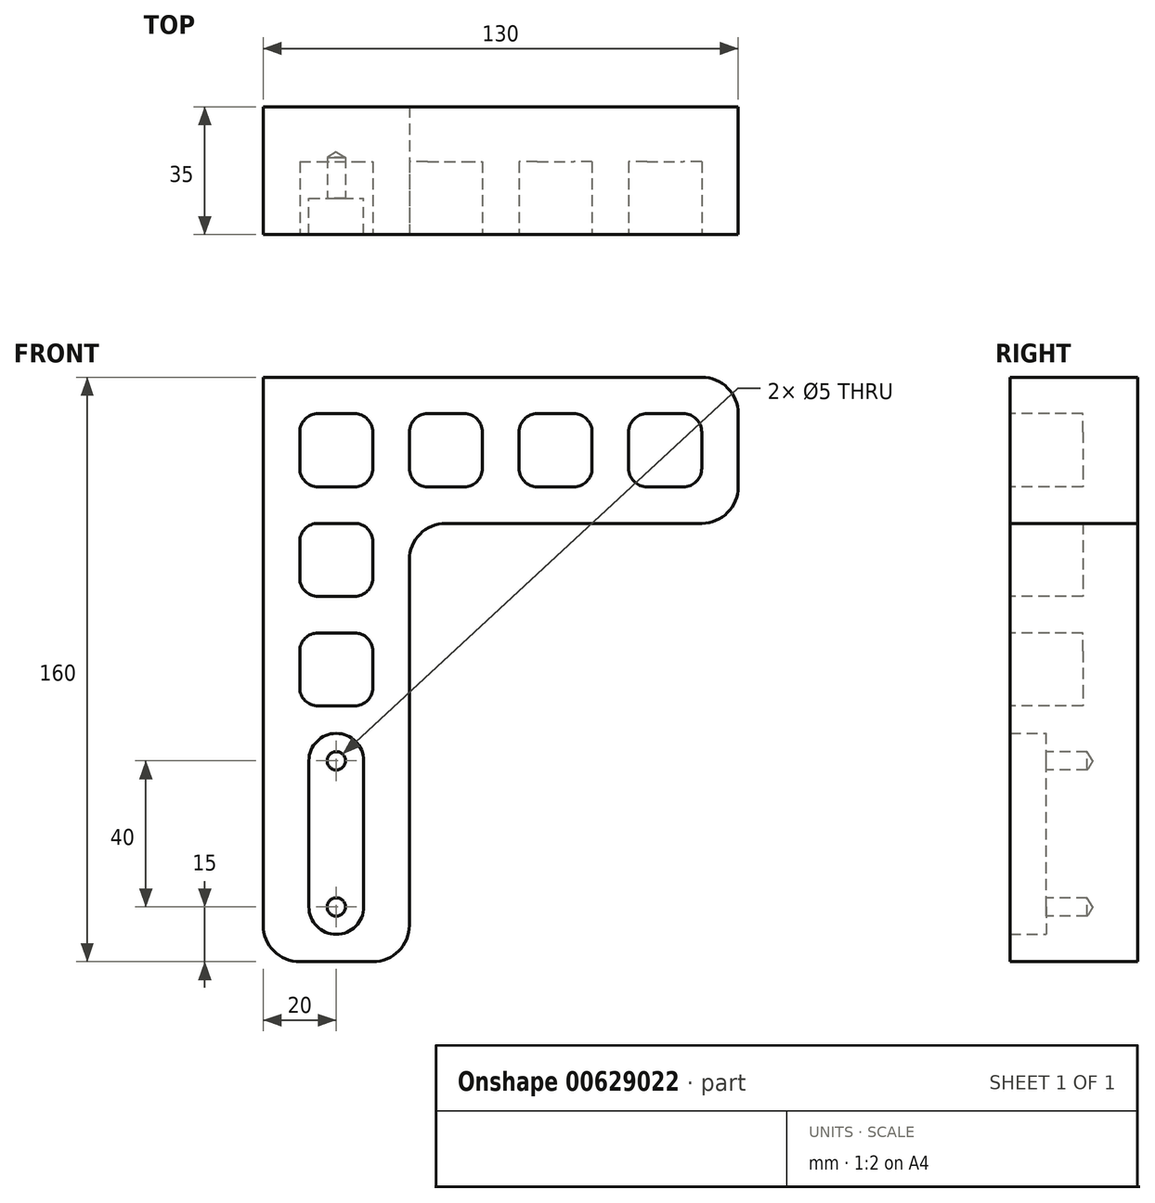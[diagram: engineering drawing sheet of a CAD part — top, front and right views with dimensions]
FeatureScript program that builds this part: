
annotation { "Feature Type Name" : "Feature", "Feature Type Description" : "" }
export const myFeature = defineFeature(function(context is Context, id is Id, definition is map)
    precondition{}
    {
        {
            var Q0;
            Q0=qCreatedBy(makeId("Front.planeOp"),FACE);
            var sketch = newSketch(context, id + "F0", { "sketchPlane" : qUnion([Q0])});
            skLineSegment(sketch, "E0.bottom", {"start": v(0, 0) * mm, "end": v(40, 0) * mm});
            skLineSegment(sketch, "E0.top", {"start": v(0, -160) * mm, "end": v(40, -160) * mm});
            skLineSegment(sketch, "E0.left", {"start": v(0, 0) * mm, "end": v(0, -160) * mm});
            skLineSegment(sketch, "E0.right", {"start": v(40, 0) * mm, "end": v(40, -160) * mm});
            skLineSegment(sketch, "E1.bottom", {"start": v(0, 0) * mm, "end": v(10, 0) * mm});
            skLineSegment(sketch, "E1.top", {"start": v(0, -10) * mm, "end": v(10, -10) * mm});
            skLineSegment(sketch, "E1.left", {"start": v(0, 0) * mm, "end": v(0, -10) * mm});
            skLineSegment(sketch, "E1.right", {"start": v(10, 0) * mm, "end": v(10, -10) * mm});
            skLineSegment(sketch, "E2.bottom", {"start": v(15, -10) * mm, "end": v(25, -10) * mm});
            skLineSegment(sketch, "E2.top", {"start": v(15, -30) * mm, "end": v(25, -30) * mm});
            skLineSegment(sketch, "E2.left", {"start": v(10, -15) * mm, "end": v(10, -25) * mm});
            skLineSegment(sketch, "E2.right", {"start": v(30, -15) * mm, "end": v(30, -25) * mm});
            skPoint(sketch, "E3.visualSharp", {"position": v(10, -10) * mm});
            skArc(sketch, "E3.filletArc", {"start": v(15, -10) * mm, "mid": v(11.46, -11.46) * mm, "end": v(10, -15) * mm});
            skPoint(sketch, "E4.visualSharp", {"position": v(10, -30) * mm});
            skArc(sketch, "E4.filletArc", {"start": v(10, -25) * mm, "mid": v(11.46, -28.54) * mm, "end": v(15, -30) * mm});
            skPoint(sketch, "E5.visualSharp", {"position": v(30, -30) * mm});
            skArc(sketch, "E5.filletArc", {"start": v(25, -30) * mm, "mid": v(28.54, -28.54) * mm, "end": v(30, -25) * mm});
            skPoint(sketch, "E6.visualSharp", {"position": v(30, -10) * mm});
            skArc(sketch, "E6.filletArc", {"start": v(30, -15) * mm, "mid": v(28.54, -11.46) * mm, "end": v(25, -10) * mm});
            skPoint(sketch, "E7.0.1.0", {"position": v(10, -40) * mm});
            skPoint(sketch, "E7.0.1.1", {"position": v(10, -60) * mm});
            skPoint(sketch, "E7.0.1.2", {"position": v(30, -40) * mm});
            skPoint(sketch, "E7.0.1.3", {"position": v(30, -60) * mm});
            skLineSegment(sketch, "E7.0.1.4", {"start": v(15, -60) * mm, "end": v(25, -60) * mm});
            skLineSegment(sketch, "E7.0.1.5", {"start": v(15, -40) * mm, "end": v(25, -40) * mm});
            skLineSegment(sketch, "E7.0.1.6", {"start": v(10, -45) * mm, "end": v(10, -55) * mm});
            skLineSegment(sketch, "E7.0.1.7", {"start": v(30, -45) * mm, "end": v(30, -55) * mm});
            skArc(sketch, "E7.0.1.8", {"start": v(25, -60) * mm, "mid": v(28.54, -58.54) * mm, "end": v(30, -55) * mm});
            skArc(sketch, "E7.0.1.9", {"start": v(15, -40) * mm, "mid": v(11.46, -41.46) * mm, "end": v(10, -45) * mm});
            skArc(sketch, "E7.0.1.10", {"start": v(30, -45) * mm, "mid": v(28.54, -41.46) * mm, "end": v(25, -40) * mm});
            skArc(sketch, "E7.0.1.11", {"start": v(10, -55) * mm, "mid": v(11.46, -58.54) * mm, "end": v(15, -60) * mm});
            skPoint(sketch, "E7.0.2.0", {"position": v(10, -70) * mm});
            skPoint(sketch, "E7.0.2.1", {"position": v(10, -90) * mm});
            skPoint(sketch, "E7.0.2.2", {"position": v(30, -70) * mm});
            skPoint(sketch, "E7.0.2.3", {"position": v(30, -90) * mm});
            skLineSegment(sketch, "E7.0.2.4", {"start": v(15, -90) * mm, "end": v(25, -90) * mm});
            skLineSegment(sketch, "E7.0.2.5", {"start": v(15, -70) * mm, "end": v(25, -70) * mm});
            skLineSegment(sketch, "E7.0.2.6", {"start": v(10, -75) * mm, "end": v(10, -85) * mm});
            skLineSegment(sketch, "E7.0.2.7", {"start": v(30, -75) * mm, "end": v(30, -85) * mm});
            skArc(sketch, "E7.0.2.8", {"start": v(25, -90) * mm, "mid": v(28.54, -88.54) * mm, "end": v(30, -85) * mm});
            skArc(sketch, "E7.0.2.9", {"start": v(15, -70) * mm, "mid": v(11.46, -71.46) * mm, "end": v(10, -75) * mm});
            skArc(sketch, "E7.0.2.10", {"start": v(30, -75) * mm, "mid": v(28.54, -71.46) * mm, "end": v(25, -70) * mm});
            skArc(sketch, "E7.0.2.11", {"start": v(10, -85) * mm, "mid": v(11.46, -88.54) * mm, "end": v(15, -90) * mm});
            skPoint(sketch, "E7.1.0.0", {"position": v(40, -10) * mm});
            skPoint(sketch, "E7.1.0.1", {"position": v(40, -30) * mm});
            skPoint(sketch, "E7.1.0.2", {"position": v(60, -10) * mm});
            skPoint(sketch, "E7.1.0.3", {"position": v(60, -30) * mm});
            skLineSegment(sketch, "E7.1.0.4", {"start": v(45, -30) * mm, "end": v(55, -30) * mm});
            skLineSegment(sketch, "E7.1.0.5", {"start": v(45, -10) * mm, "end": v(55, -10) * mm});
            skLineSegment(sketch, "E7.1.0.6", {"start": v(40, -15) * mm, "end": v(40, -25) * mm});
            skLineSegment(sketch, "E7.1.0.7", {"start": v(60, -15) * mm, "end": v(60, -25) * mm});
            skArc(sketch, "E7.1.0.8", {"start": v(55, -30) * mm, "mid": v(58.54, -28.54) * mm, "end": v(60, -25) * mm});
            skArc(sketch, "E7.1.0.9", {"start": v(45, -10) * mm, "mid": v(41.46, -11.46) * mm, "end": v(40, -15) * mm});
            skArc(sketch, "E7.1.0.10", {"start": v(60, -15) * mm, "mid": v(58.54, -11.46) * mm, "end": v(55, -10) * mm});
            skArc(sketch, "E7.1.0.11", {"start": v(40, -25) * mm, "mid": v(41.46, -28.54) * mm, "end": v(45, -30) * mm});
            skLineSegment(sketch, "E7.1.1.5", {"start": v(45, -40) * mm, "end": v(55, -40) * mm});
            skLineSegment(sketch, "E7.1.1.6", {"start": v(40, -45) * mm, "end": v(40, -55) * mm});
            skLineSegment(sketch, "E7.1.2.6", {"start": v(40, -75) * mm, "end": v(40, -85) * mm});
            skPoint(sketch, "E7.2.0.0", {"position": v(70, -10) * mm});
            skPoint(sketch, "E7.2.0.1", {"position": v(70, -30) * mm});
            skPoint(sketch, "E7.2.0.2", {"position": v(90, -10) * mm});
            skPoint(sketch, "E7.2.0.3", {"position": v(90, -30) * mm});
            skLineSegment(sketch, "E7.2.0.4", {"start": v(75, -30) * mm, "end": v(85, -30) * mm});
            skLineSegment(sketch, "E7.2.0.5", {"start": v(75, -10) * mm, "end": v(85, -10) * mm});
            skLineSegment(sketch, "E7.2.0.6", {"start": v(70, -15) * mm, "end": v(70, -25) * mm});
            skLineSegment(sketch, "E7.2.0.7", {"start": v(90, -15) * mm, "end": v(90, -25) * mm});
            skArc(sketch, "E7.2.0.8", {"start": v(85, -30) * mm, "mid": v(88.54, -28.54) * mm, "end": v(90, -25) * mm});
            skArc(sketch, "E7.2.0.9", {"start": v(75, -10) * mm, "mid": v(71.46, -11.46) * mm, "end": v(70, -15) * mm});
            skArc(sketch, "E7.2.0.10", {"start": v(90, -15) * mm, "mid": v(88.54, -11.46) * mm, "end": v(85, -10) * mm});
            skArc(sketch, "E7.2.0.11", {"start": v(70, -25) * mm, "mid": v(71.46, -28.54) * mm, "end": v(75, -30) * mm});
            skLineSegment(sketch, "E7.2.1.5", {"start": v(75, -40) * mm, "end": v(85, -40) * mm});
            skPoint(sketch, "E7.3.0.0", {"position": v(100, -10) * mm});
            skPoint(sketch, "E7.3.0.1", {"position": v(100, -30) * mm});
            skPoint(sketch, "E7.3.0.2", {"position": v(120, -10) * mm});
            skPoint(sketch, "E7.3.0.3", {"position": v(120, -30) * mm});
            skLineSegment(sketch, "E7.3.0.4", {"start": v(105, -30) * mm, "end": v(115, -30) * mm});
            skLineSegment(sketch, "E7.3.0.5", {"start": v(105, -10) * mm, "end": v(115, -10) * mm});
            skLineSegment(sketch, "E7.3.0.6", {"start": v(100, -15) * mm, "end": v(100, -25) * mm});
            skLineSegment(sketch, "E7.3.0.7", {"start": v(120, -15) * mm, "end": v(120, -25) * mm});
            skArc(sketch, "E7.3.0.8", {"start": v(115, -30) * mm, "mid": v(118.54, -28.54) * mm, "end": v(120, -25) * mm});
            skArc(sketch, "E7.3.0.9", {"start": v(105, -10) * mm, "mid": v(101.46, -11.46) * mm, "end": v(100, -15) * mm});
            skArc(sketch, "E7.3.0.10", {"start": v(120, -15) * mm, "mid": v(118.54, -11.46) * mm, "end": v(115, -10) * mm});
            skArc(sketch, "E7.3.0.11", {"start": v(100, -25) * mm, "mid": v(101.46, -28.54) * mm, "end": v(105, -30) * mm});
            skLineSegment(sketch, "E7.3.1.5", {"start": v(105, -40) * mm, "end": v(115, -40) * mm});
            skLineSegment(sketch, "E7.direction1", {"start": v(10, -30) * mm, "end": v(40, -30) * mm, "construction": true});
            skLineSegment(sketch, "E7.direction2", {"start": v(10, -30) * mm, "end": v(10, -60) * mm, "construction": true});
            skLineSegment(sketch, "E8.bottom", {"start": v(0, 0) * mm, "end": v(130, 0) * mm});
            skLineSegment(sketch, "E8.top", {"start": v(0, -40) * mm, "end": v(130, -40) * mm});
            skLineSegment(sketch, "E8.left", {"start": v(0, 0) * mm, "end": v(0, -40) * mm});
            skLineSegment(sketch, "E8.right", {"start": v(130, 0) * mm, "end": v(130, -40) * mm});
            skSolve(sketch);
        }
        {
            var Q0;
            {var subQ7=sQuery(id+"F0.wireOp",EDGE,"E0.top");Q0=makeQuery(id+"F0.imprint","IMPRINT",FACE,{"disambiguationData":[TD([[makeQuery(id+"F0.imprint","IMPRINT",EDGE,{"derivedFrom":subQ7}),1.0]])]});}
            var Q1;
            {var subQ5=sQuery(id+"F0.wireOp",EDGE,"E1.top");Q1=makeQuery(id+"F0.imprint","IMPRINT",FACE,{"disambiguationData":[TD([[makeQuery(id+"F0.imprint","IMPRINT",EDGE,{"derivedFrom":subQ5}),-1.0]])]});}
            var Q2;
            {var subQ0=sQuery(id+"F0.wireOp",EDGE,"E1.top");Q2=makeQuery(id+"F0.imprint","IMPRINT",FACE,{"disambiguationData":[TD([[makeQuery(id+"F0.imprint","IMPRINT",EDGE,{"derivedFrom":subQ0}),1.0]])]});}
            var Q3;
            Q3=makeQuery(id+"F0.imprint","IMPRINT",FACE,{"disambiguationData":[TD([[makeQuery(id+"F0.imprint","IMPRINT",EDGE,{"derivedFrom":sQuery(id+"F0.wireOp",EDGE,"E7.1.0.4")}),-1.0]])]});
            var Q4;
            Q4=makeQuery(id+"F0.imprint","IMPRINT",FACE,{"disambiguationData":[TD([[makeQuery(id+"F0.imprint","IMPRINT",EDGE,{"derivedFrom":sQuery(id+"F0.wireOp",EDGE,"E7.0.2.4")}),1.0]])]});
            var Q5;
            Q5=makeQuery(id+"F0.imprint","IMPRINT",FACE,{"disambiguationData":[TD([[makeQuery(id+"F0.imprint","IMPRINT",EDGE,{"derivedFrom":sQuery(id+"F0.wireOp",EDGE,"E7.0.1.4")}),1.0]])]});
            var Q6;
            Q6=makeQuery(id+"F0.imprint","IMPRINT",FACE,{"disambiguationData":[TD([[makeQuery(id+"F0.imprint","IMPRINT",EDGE,{"derivedFrom":sQuery(id+"F0.wireOp",EDGE,"E2.bottom")}),-1.0]])]});
            var Q7;
            Q7=makeQuery(id+"F0.imprint","IMPRINT",FACE,{"disambiguationData":[TD([[makeQuery(id+"F0.imprint","IMPRINT",EDGE,{"derivedFrom":sQuery(id+"F0.wireOp",EDGE,"E7.1.0.4")}),1.0]])]});
            var Q8;
            Q8=makeQuery(id+"F0.imprint","IMPRINT",FACE,{"disambiguationData":[TD([[makeQuery(id+"F0.imprint","IMPRINT",EDGE,{"derivedFrom":sQuery(id+"F0.wireOp",EDGE,"E7.2.0.4")}),1.0]])]});
            var Q9;
            Q9=makeQuery(id+"F0.imprint","IMPRINT",FACE,{"disambiguationData":[TD([[makeQuery(id+"F0.imprint","IMPRINT",EDGE,{"derivedFrom":sQuery(id+"F0.wireOp",EDGE,"E7.3.0.4")}),1.0]])]});
            extrude(context, id + "F1", {"entities" : qUnion([Q0, Q1, Q2, Q3, Q4, Q5, Q6, Q7, Q8, Q9]), "oppositeDirection" : true, "depth" : 25 * mm, "offsetDistance" : 25 * mm});
        }
        {
            var Q0;
            Q0=makeQuery(id+"F0.imprint","IMPRINT",FACE,{"disambiguationData":[TD([[makeQuery(id+"F0.imprint","IMPRINT",EDGE,{"derivedFrom":sQuery(id+"F0.wireOp",EDGE,"E2.bottom")}),-1.0]])]});
            var Q1;
            Q1=makeQuery(id+"F0.imprint","IMPRINT",FACE,{"disambiguationData":[TD([[makeQuery(id+"F0.imprint","IMPRINT",EDGE,{"derivedFrom":sQuery(id+"F0.wireOp",EDGE,"E7.1.0.4")}),1.0]])]});
            var Q2;
            Q2=makeQuery(id+"F0.imprint","IMPRINT",FACE,{"disambiguationData":[TD([[makeQuery(id+"F0.imprint","IMPRINT",EDGE,{"derivedFrom":sQuery(id+"F0.wireOp",EDGE,"E7.2.0.4")}),1.0]])]});
            var Q3;
            Q3=makeQuery(id+"F0.imprint","IMPRINT",FACE,{"disambiguationData":[TD([[makeQuery(id+"F0.imprint","IMPRINT",EDGE,{"derivedFrom":sQuery(id+"F0.wireOp",EDGE,"E7.3.0.4")}),1.0]])]});
            var Q4;
            Q4=makeQuery(id+"F0.imprint","IMPRINT",FACE,{"disambiguationData":[TD([[makeQuery(id+"F0.imprint","IMPRINT",EDGE,{"derivedFrom":sQuery(id+"F0.wireOp",EDGE,"E7.0.1.4")}),1.0]])]});
            var Q5;
            Q5=makeQuery(id+"F0.imprint","IMPRINT",FACE,{"disambiguationData":[TD([[makeQuery(id+"F0.imprint","IMPRINT",EDGE,{"derivedFrom":sQuery(id+"F0.wireOp",EDGE,"E7.0.2.4")}),1.0]])]});
            extrude(context, id + "F2", {"entities" : qUnion([Q0, Q1, Q2, Q3, Q4, Q5]), "operationType" : NewBodyOperationType.REMOVE, "oppositeDirection" : true, "depth" : 10 * mm, "offsetDistance" : 25 * mm});
        }
        {
            var Q0;
            Q0=makeQuery(id+"F1.opExtrude","SWEPT_EDGE",EDGE,{"disambiguationData":[OSD([sQuery(id+"F0.wireOp",EDGE,"E0.top"),sQuery(id+"F0.wireOp",EDGE,"E0.left")])]});
            var Q1;
            Q1=makeQuery(id+"F1.opExtrude","SWEPT_EDGE",EDGE,{"disambiguationData":[OSD([sQuery(id+"F0.wireOp",EDGE,"E0.top"),sQuery(id+"F0.wireOp",EDGE,"E0.right")])]});
            var Q2;
            Q2=makeQuery(id+"F1.opExtrude","SWEPT_EDGE",EDGE,{"disambiguationData":[OSD([sQuery(id+"F0.wireOp",EDGE,"E0.right"),sQuery(id+"F0.wireOp",EDGE,"E8.top")])]});
            var Q3;
            Q3=makeQuery(id+"F1.opExtrude","SWEPT_EDGE",EDGE,{"disambiguationData":[OSD([sQuery(id+"F0.wireOp",EDGE,"E8.top"),sQuery(id+"F0.wireOp",EDGE,"E8.right")])]});
            var Q4;
            Q4=makeQuery(id+"F1.opExtrude","SWEPT_EDGE",EDGE,{"disambiguationData":[OSD([sQuery(id+"F0.wireOp",EDGE,"E8.bottom"),sQuery(id+"F0.wireOp",EDGE,"E8.right")])]});
            var Q5;
            Q5=makeQuery(id+"F1.opExtrude","SWEPT_EDGE",EDGE,{"disambiguationData":[OSD([sQuery(id+"F0.wireOp",EDGE,"E8.bottom"),sQuery(id+"F0.wireOp",EDGE,"E8.left")])]});
            fillet(context, id + "F3", {"entities" : qUnion([Q0, Q1, Q2, Q3, Q4, Q5]), "radius" : 10 * mm, "tangentPropagation" : true, "allowEdgeOverflow" : false});
        }
        {
            var Q0;
            Q0=makeQuery(id+"F1.opExtrude","CAP_FACE",FACE,{"disambiguationData":[OSD([sQuery(id+"F0.wireOp",EDGE,"E0.top"),sQuery(id+"F0.wireOp",EDGE,"E0.left"),sQuery(id+"F0.wireOp",EDGE,"E0.right"),sQuery(id+"F0.wireOp",EDGE,"E7.1.1.6"),sQuery(id+"F0.wireOp",EDGE,"E7.1.2.6"),sQuery(id+"F0.wireOp",EDGE,"E8.bottom"),sQuery(id+"F0.wireOp",EDGE,"E8.top"),sQuery(id+"F0.wireOp",EDGE,"E8.left"),sQuery(id+"F0.wireOp",EDGE,"E8.right")])],"isStart":true});
            var sketch = newSketch(context, id + "F4", { "sketchPlane" : qUnion([Q0])});
            skLineSegment(sketch, "E9", {"start": v(20, -160) * mm, "end": v(20, -145) * mm});
            skLineSegment(sketch, "E10", {"start": v(20, -145) * mm, "end": v(20, -105) * mm});
            skPoint(sketch, "E10.endSnap0", {"position": v(20, -152.5) * mm});
            skArc(sketch, "E11.0.startCap", {"start": v(27.5, -145) * mm, "mid": v(20, -152.5) * mm, "end": v(12.5, -145) * mm});
            skArc(sketch, "E11.0.endCap", {"start": v(12.5, -105) * mm, "mid": v(20, -97.5) * mm, "end": v(27.5, -105) * mm});
            skLineSegment(sketch, "E11.0.left", {"start": v(12.5, -145) * mm, "end": v(12.5, -105) * mm});
            skLineSegment(sketch, "E11.0.right", {"start": v(27.5, -145) * mm, "end": v(27.5, -105) * mm});
            skSolve(sketch);
        }
        {
            var Q0;
            Q0=makeQuery(id+"F4.imprint","IMPRINT",FACE,{"disambiguationData":[TD([[makeQuery(id+"F4.imprint","IMPRINT",EDGE,{"derivedFrom":sQuery(id+"F4.wireOp",EDGE,"E11.0.endCap")}),-1.0]])]});
            extrude(context, id + "F5", {"entities" : qUnion([Q0]), "operationType" : NewBodyOperationType.ADD, "depth" : 10 * mm, "offsetDistance" : 25 * mm});
        }
        {
            var Q0;
            Q0=makeQuery(id+"F5.opExtrude","CAP_FACE",FACE,{"disambiguationData":[OSD([sQuery(id+"F4.wireOp",EDGE,"E11.0.startCap"),sQuery(id+"F4.wireOp",EDGE,"E11.0.endCap"),sQuery(id+"F4.wireOp",EDGE,"E11.0.left"),sQuery(id+"F4.wireOp",EDGE,"E11.0.right")])],"isStart":false});
            var sketch = newSketch(context, id + "F6", { "sketchPlane" : qUnion([Q0])});
            skPoint(sketch, "E12", {"position": v(20, -105) * mm});
            skPoint(sketch, "E13", {"position": v(20, -145) * mm});
            skSolve(sketch);
        }
        {
            var Q0;
            Q0=sQuery(id+"F6.wireOp",VERTEX,"E12");
            var Q1;
            Q1=sQuery(id+"F6.wireOp",VERTEX,"E13");
            var Q2;
            Q2=makeQuery(id+"F1.opExtrude","SWEPT_BODY",BODY,{"disambiguationData":[OSD([sQuery(id+"F0.wireOp",EDGE,"E0.top"),sQuery(id+"F0.wireOp",EDGE,"E0.left"),sQuery(id+"F0.wireOp",EDGE,"E0.right"),sQuery(id+"F0.wireOp",EDGE,"E7.1.1.6"),sQuery(id+"F0.wireOp",EDGE,"E7.1.2.6"),sQuery(id+"F0.wireOp",EDGE,"E8.bottom"),sQuery(id+"F0.wireOp",EDGE,"E8.top"),sQuery(id+"F0.wireOp",EDGE,"E8.left"),sQuery(id+"F0.wireOp",EDGE,"E8.right")])]});
            hole(context, id + "F7", {"style" : HoleStyle.SIMPLE, "endStyle" : HoleEndStyle.BLIND, "standardTappedOrClearance" : lookupTablePath({ "standard" : "ISO", "engagement" : "75%", "pitch" : "1 mm", "size" : "M6", "type" : "Tapped" }), "standardBlindInLast" : lookupTablePath({ "standard" : "ISO", "engagement" : "75%", "pitch" : "1 mm", "size" : "M6", "type" : "Tapped" }), "holeDiameter" : 5 * mm, "majorDiameter" : 6 * mm, "showTappedDepth" : true, "holeDepth" : 11.2 * mm, "isTappedThrough" : true, "tappedDepth" : 8.2 * mm, "tapClearance" : 3, "locations" : qUnion([Q0, Q1]), "scope" : qUnion([Q2])});
        }
    });
